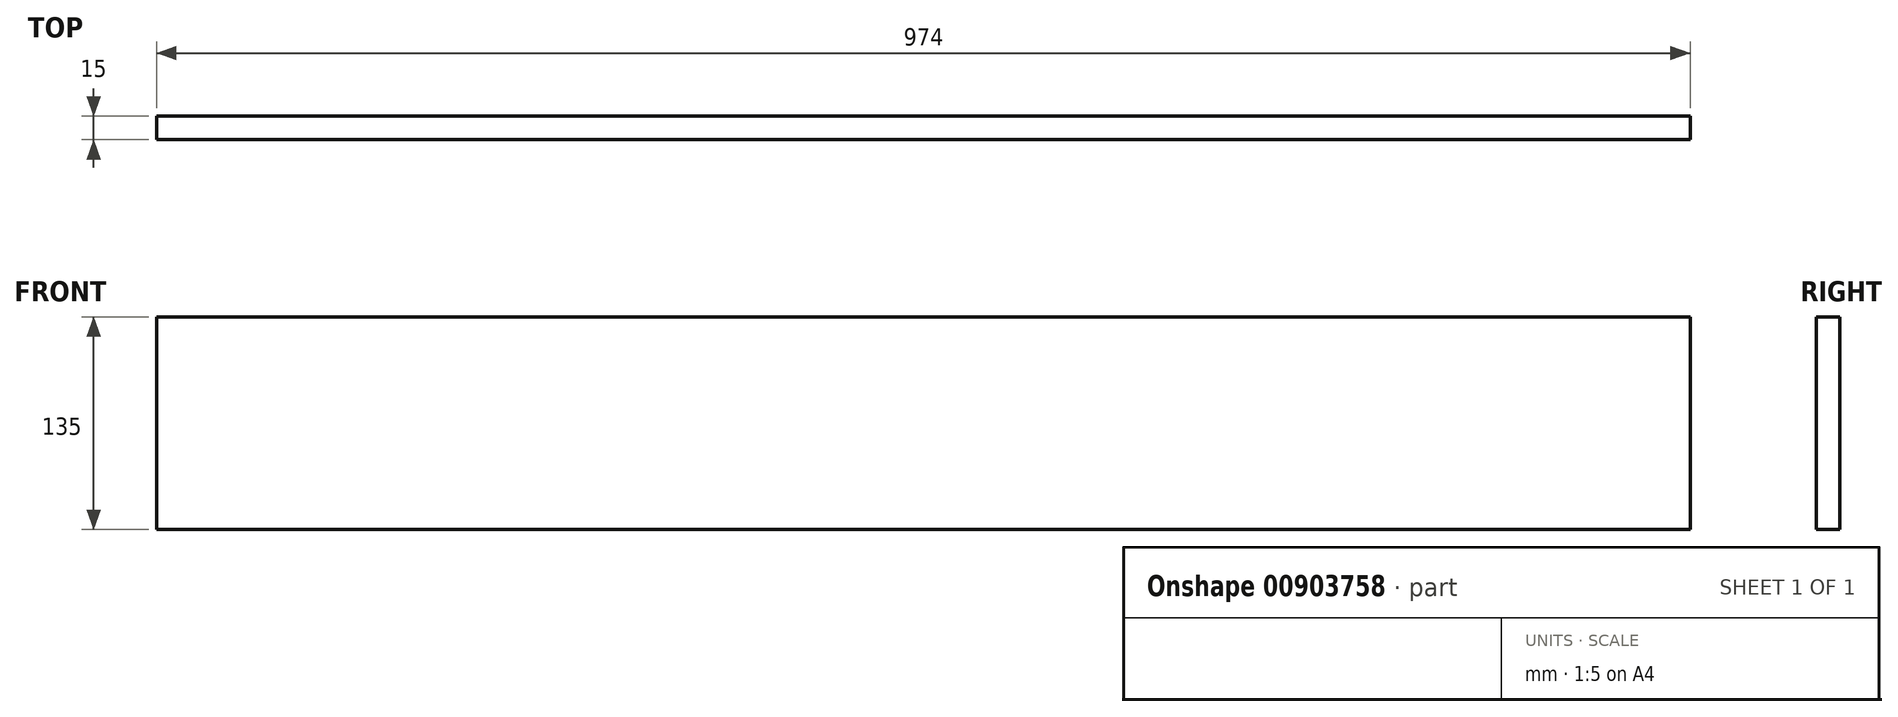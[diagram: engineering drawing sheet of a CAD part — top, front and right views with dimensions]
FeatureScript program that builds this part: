
annotation { "Feature Type Name" : "Feature", "Feature Type Description" : "" }
export const myFeature = defineFeature(function(context is Context, id is Id, definition is map)
    precondition{}
    {
        {
            var Q0;
            Q0=qCreatedBy(makeId("Front.planeOp"),FACE);
            var sketch = newSketch(context, id + "F0", { "sketchPlane" : qUnion([Q0])});
            skLineSegment(sketch, "E0.bottom", {"start": v(-487, 67.5) * mm, "end": v(487, 67.5) * mm});
            skLineSegment(sketch, "E0.top", {"start": v(-487, -67.5) * mm, "end": v(487, -67.5) * mm});
            skLineSegment(sketch, "E0.left", {"start": v(-487, 67.5) * mm, "end": v(-487, -67.5) * mm});
            skLineSegment(sketch, "E0.right", {"start": v(487, 67.5) * mm, "end": v(487, -67.5) * mm});
            skSolve(sketch);
        }
        {
            var Q0;
            Q0=makeQuery(id+"F0.imprint","IMPRINT",FACE,{"disambiguationData":[TD([[makeQuery(id+"F0.imprint","IMPRINT",EDGE,{"derivedFrom":sQuery(id+"F0.wireOp",EDGE,"E0.bottom")}),-1.0]])]});
            extrude(context, id + "F1", {"entities" : qUnion([Q0]), "depth" : 15 * mm, "offsetDistance" : 25 * mm});
        }
    });
